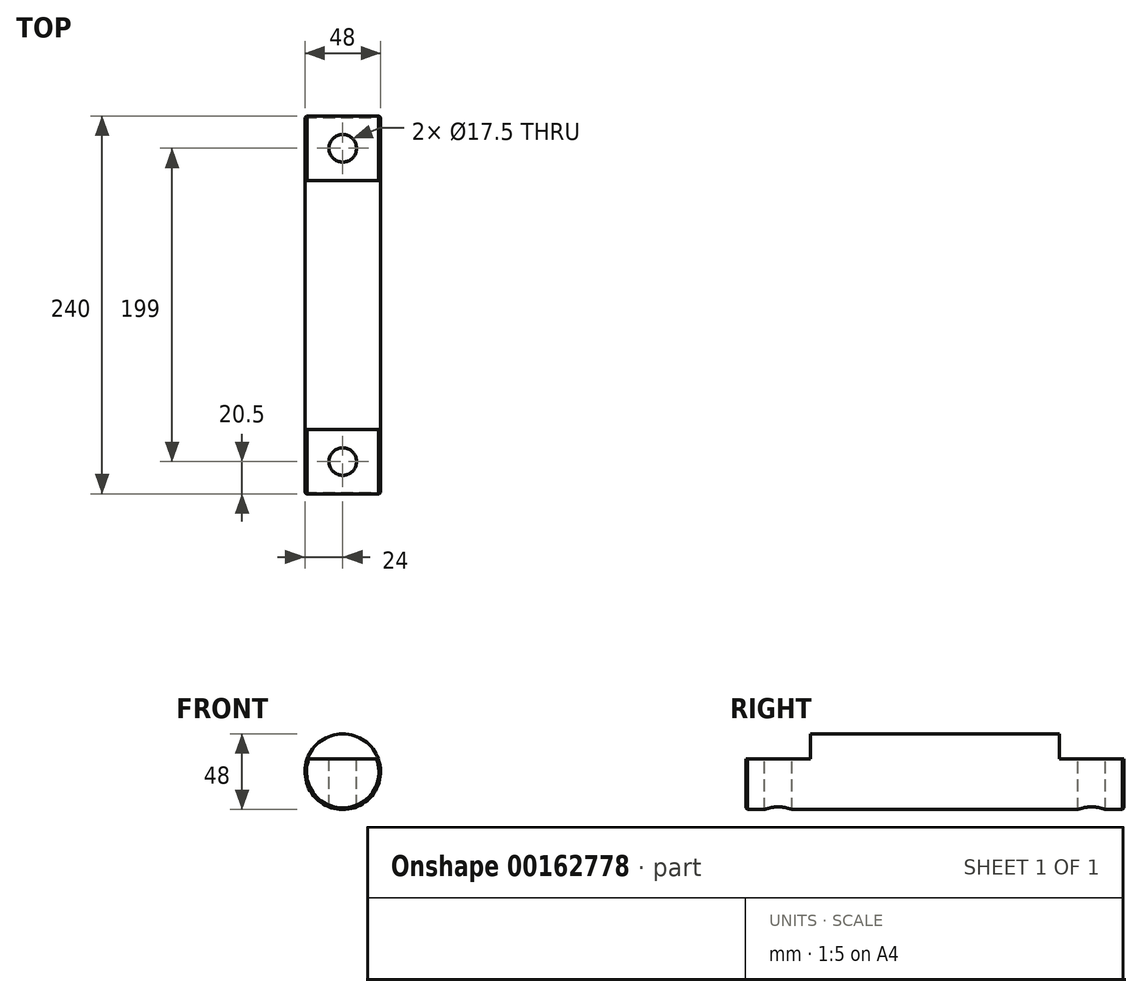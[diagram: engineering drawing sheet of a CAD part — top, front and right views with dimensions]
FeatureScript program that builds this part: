
annotation { "Feature Type Name" : "Feature", "Feature Type Description" : "" }
export const myFeature = defineFeature(function(context is Context, id is Id, definition is map)
    precondition{}
    {
        {
            var Q0;
            Q0=qCreatedBy(makeId("Front.planeOp"),FACE);
            var sketch = newSketch(context, id + "F0", { "sketchPlane" : qUnion([Q0])});
            skCircle(sketch, "E0", {"center": v(0, 0) * mm, "radius": 24 * mm});
            skSolve(sketch);
        }
        {
            var Q0;
            Q0 = qSketchRegion(id + "F0", true);
            extrude(context, id + "F1", {"entities" : qUnion([Q0]), "depth" : 240 * mm});
        }
        {
            var Q0;
            Q0=makeQuery(id+"F1.opExtrude","SWEPT_FACE",FACE,{"disambiguationData":[OSD([sQuery(id+"F0.wireOp",EDGE,"E0")])]});
            chamfer(context, id + "F2", {"entities" : qUnion([Q0]), "width" : 1 * mm, "tangentPropagation" : true});
        }
        {
            var Q0;
            Q0=qCreatedBy(makeId("Top.planeOp"),FACE);
            var sketch = newSketch(context, id + "F3", { "sketchPlane" : qUnion([Q0])});
            skLineSegment(sketch, "E1.bottom", {"start": v(25, -42.5) * mm, "end": v(-25, -42.5) * mm});
            skLineSegment(sketch, "E1.top", {"start": v(25, 0) * mm, "end": v(-25, 0) * mm});
            skLineSegment(sketch, "E1.left", {"start": v(25, -42.5) * mm, "end": v(25, 0) * mm});
            skLineSegment(sketch, "E1.right", {"start": v(-25, -42.5) * mm, "end": v(-25, 0) * mm});
            skLineSegment(sketch, "E2.bottom", {"start": v(25, -197.5) * mm, "end": v(-25, -197.5) * mm});
            skLineSegment(sketch, "E2.top", {"start": v(25, -240) * mm, "end": v(-25, -240) * mm});
            skLineSegment(sketch, "E2.left", {"start": v(25, -197.5) * mm, "end": v(25, -240) * mm});
            skLineSegment(sketch, "E2.right", {"start": v(-25, -197.5) * mm, "end": v(-25, -240) * mm});
            skPoint(sketch, "E3", {"position": v(0, -240) * mm});
            skSolve(sketch);
        }
        {
            var Q0;
            Q0=qCreatedBy(makeId("Top.planeOp"),FACE);
            cPlane(context, id + "F4", {"entities" : qUnion([Q0]), "cplaneType" : CPlaneType.OFFSET, "offset" : 8 * mm, "width" : 150 * mm, "height" : 150 * mm});
        }
        {
            var Q0;
            Q0=qCreatedBy(id+"F4.planeOp",FACE);
            var sketch = newSketch(context, id + "F5", { "sketchPlane" : qUnion([Q0])});
            skLineSegment(sketch, "E4.bottom", {"start": v(25, -41) * mm, "end": v(-25, -41) * mm});
            skLineSegment(sketch, "E4.top", {"start": v(25, 0) * mm, "end": v(-25, 0) * mm});
            skLineSegment(sketch, "E4.left", {"start": v(25, -41) * mm, "end": v(25, 0) * mm});
            skLineSegment(sketch, "E4.right", {"start": v(-25, -41) * mm, "end": v(-25, 0) * mm});
            skLineSegment(sketch, "E5.bottom", {"start": v(25, -199) * mm, "end": v(-25, -199) * mm});
            skLineSegment(sketch, "E5.top", {"start": v(25, -240) * mm, "end": v(-25, -240) * mm});
            skLineSegment(sketch, "E5.left", {"start": v(25, -199) * mm, "end": v(25, -240) * mm});
            skLineSegment(sketch, "E5.right", {"start": v(-25, -199) * mm, "end": v(-25, -240) * mm});
            skPoint(sketch, "E6", {"position": v(0, -240) * mm});
            skSolve(sketch);
        }
        {
            var Q0;
            Q0 = qSketchRegion(id + "F5", true);
            extrude(context, id + "F6", {"entities" : qUnion([Q0]), "operationType" : NewBodyOperationType.REMOVE, "depth" : 125 * mm});
        }
        {
            var Q0;
            Q0=makeQuery(id+"F6.boolean.opBoolean","COPY",FACE,{"derivedFrom":makeQuery(id+"F6.opExtrude","CAP_FACE",FACE,{"disambiguationData":[OSD([sQuery(id+"F5.wireOp",EDGE,"E4.bottom"),sQuery(id+"F5.wireOp",EDGE,"E4.top"),sQuery(id+"F5.wireOp",EDGE,"E4.left"),sQuery(id+"F5.wireOp",EDGE,"E4.right")])],"isStart":true})});
            var sketch = newSketch(context, id + "F7", { "sketchPlane" : qUnion([Q0])});
            skPoint(sketch, "E7", {"position": v(0, -20.5) * mm});
            skPoint(sketch, "E8", {"position": v(0, -219.5) * mm});
            skLineSegment(sketch, "E9", {"start": v(0, 0) * mm, "end": v(0, -41) * mm, "construction": true});
            skLineSegment(sketch, "E10", {"start": v(0, -240) * mm, "end": v(0, -199) * mm, "construction": true});
            skSolve(sketch);
        }
        {
            var Q0;
            Q0=sQuery(id+"F7.wireOp",VERTEX,"E7");
            var Q1;
            Q1=sQuery(id+"F7.wireOp",VERTEX,"E8");
            var Q2;
            Q2=makeQuery(id+"F1.opExtrude","SWEPT_BODY",BODY,{"disambiguationData":[OSD([sQuery(id+"F0.wireOp",EDGE,"E0")])]});
            hole(context, id + "F8", {"style" : HoleStyle.SIMPLE, "endStyle" : HoleEndStyle.THROUGH, "standardTappedOrClearance" : lookupTablePath({ "standard" : "ISO", "fit" : "Normal", "size" : "M16", "type" : "Clearance" }), "standardBlindInLast" : lookupTablePath({ "fit" : "Standard", "standard" : "ISO", "size" : "M16", "type" : "Clearance" }), "holeDiameter" : 17.5 * mm, "locations" : qUnion([Q0, Q1]), "scope" : qUnion([Q2]), "isTappedThrough" : true});
        }
    });
